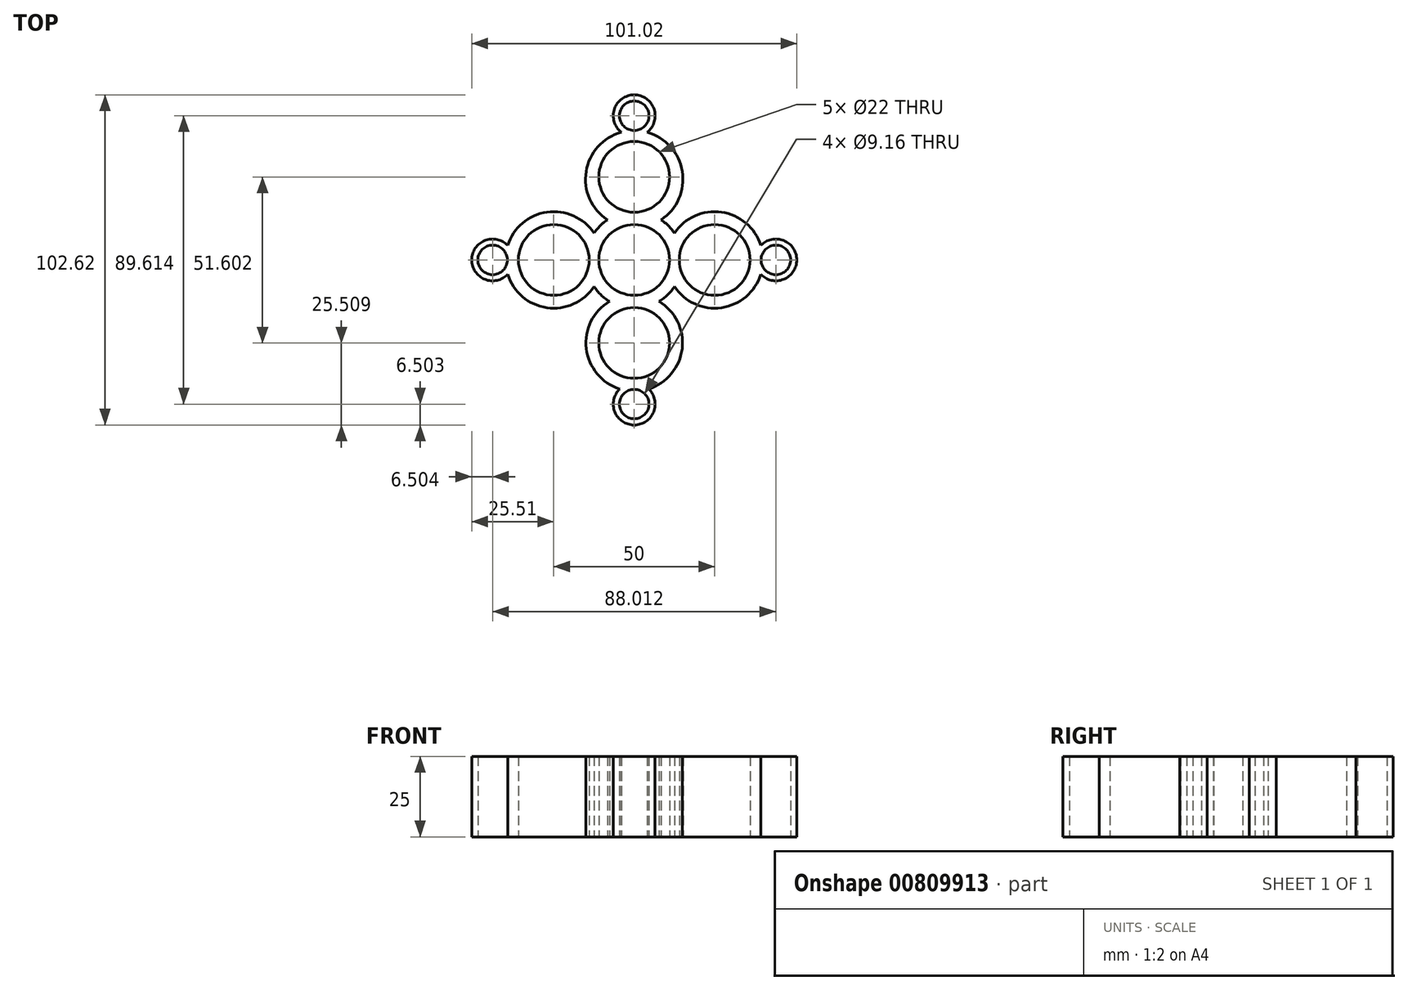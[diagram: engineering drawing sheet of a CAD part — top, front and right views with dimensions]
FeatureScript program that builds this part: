
annotation { "Feature Type Name" : "Feature", "Feature Type Description" : "" }
export const myFeature = defineFeature(function(context is Context, id is Id, definition is map)
    precondition{}
    {
        {
            var Q0;
            Q0=qCreatedBy(makeId("Top.planeOp"),FACE);
            var sketch = newSketch(context, id + "F0", { "sketchPlane" : qUnion([Q0])});
            skArc(sketch, "E0", {"start": v(0, 11) * mm, "mid": v(-11, 0) * mm, "end": v(0, -11) * mm});
            skArc(sketch, "E1", {"start": v(-12.5, -8.3) * mm, "mid": v(-10.34, -10.87) * mm, "end": v(-7.65, -12.9) * mm});
            skArc(sketch, "E2", {"start": v(-14.58, 3.52) * mm, "mid": v(-36, 0) * mm, "end": v(-14.58, -3.52) * mm});
            skArc(sketch, "E3.trimOffspring", {"start": v(-12.5, 8.3) * mm, "mid": v(-27.1, 14.85) * mm, "end": v(-39.31, 4.5) * mm});
            skArc(sketch, "E4", {"start": v(-14.58, -3.52) * mm, "mid": v(-14, 0) * mm, "end": v(-14.58, 3.52) * mm});
            skLineSegment(sketch, "E5", {"start": v(0, -11) * mm, "end": v(0, -15) * mm});
            skArc(sketch, "E6.trimOffspring", {"start": v(0, 15) * mm, "mid": v(-0.8, 14.98) * mm, "end": v(-1.59, 14.92) * mm});
            skPoint(sketch, "E7.orphan", {"position": v(0, 21.55) * mm});
            skArc(sketch, "E8.MirrorCS", {"start": v(12.5, 8.3) * mm, "mid": v(27.1, 14.85) * mm, "end": v(39.31, 4.5) * mm});
            skArc(sketch, "E9.MirrorCS", {"start": v(14.58, 3.52) * mm, "mid": v(36, 0) * mm, "end": v(14.58, -3.52) * mm});
            skArc(sketch, "E10.MirrorCS", {"start": v(14.58, -3.52) * mm, "mid": v(14, 0) * mm, "end": v(14.58, 3.52) * mm});
            skArc(sketch, "E11.MirrorCS", {"start": v(0, 11) * mm, "mid": v(11, 0) * mm, "end": v(0, -11) * mm});
            skArc(sketch, "E12.MirrorCS", {"start": v(0, 15) * mm, "mid": v(0.8, 14.98) * mm, "end": v(1.59, 14.92) * mm});
            skArc(sketch, "E13.MirrorCS", {"start": v(12.5, -8.3) * mm, "mid": v(10.34, -10.87) * mm, "end": v(7.65, -12.9) * mm});
            skArc(sketch, "E14", {"start": v(-39.31, 4.5) * mm, "mid": v(-50.5, 0) * mm, "end": v(-39.31, -4.5) * mm});
            skCircle(sketch, "E15", {"center": v(-44, 0) * mm, "radius": 4.58 * mm});
            skArc(sketch, "E16.trimOffspring", {"start": v(-39.31, -4.5) * mm, "mid": v(-27.1, -14.85) * mm, "end": v(-12.5, -8.3) * mm});
            skArc(sketch, "E17", {"start": v(39.31, -4.5) * mm, "mid": v(50.5, 0) * mm, "end": v(39.31, 4.5) * mm});
            skCircle(sketch, "E18", {"center": v(44, 0) * mm, "radius": 4.58 * mm});
            skArc(sketch, "E19.trimOffspring", {"start": v(39.31, -4.5) * mm, "mid": v(27.1, -14.85) * mm, "end": v(12.5, -8.3) * mm});
            skCircle(sketch, "E20", {"center": v(0, 25.8) * mm, "radius": 11 * mm});
            skArc(sketch, "E21.trimOffspring", {"start": v(8.35, 12.46) * mm, "mid": v(14.95, 27.47) * mm, "end": v(4, 39.69) * mm});
            skArc(sketch, "E22.trimOffspring", {"start": v(-8.35, 12.46) * mm, "mid": v(-10.63, 10.58) * mm, "end": v(-12.5, 8.3) * mm});
            skArc(sketch, "E23.trimOffspring", {"start": v(8.35, 12.46) * mm, "mid": v(10.63, 10.58) * mm, "end": v(12.5, 8.3) * mm});
            skLineSegment(sketch, "E24.trimOffspring", {"start": v(0, 15) * mm, "end": v(0, 14.8) * mm});
            skArc(sketch, "E25", {"start": v(4, 39.69) * mm, "mid": v(0, 51.3) * mm, "end": v(-4, 39.69) * mm});
            skCircle(sketch, "E26", {"center": v(0, 44.8) * mm, "radius": 4.58 * mm});
            skArc(sketch, "E27.trimOffspring", {"start": v(-4, 39.69) * mm, "mid": v(-14.95, 27.47) * mm, "end": v(-8.35, 12.46) * mm});
            skLineSegment(sketch, "E28", {"start": v(0, 0) * mm, "end": v(0, -11) * mm});
            skArc(sketch, "E29", {"start": v(1.59, -10.89) * mm, "mid": v(0, -10.8) * mm, "end": v(-1.59, -10.89) * mm});
            skCircle(sketch, "E30", {"center": v(0, -25.8) * mm, "radius": 11 * mm});
            skArc(sketch, "E31", {"start": v(-4.5, -40.11) * mm, "mid": v(0, -51.3) * mm, "end": v(4.5, -40.11) * mm});
            skCircle(sketch, "E32", {"center": v(0, -44.8) * mm, "radius": 4.58 * mm});
            skArc(sketch, "E33.trimOffspring", {"start": v(-1.59, -14.92) * mm, "mid": v(-0.8, -14.98) * mm, "end": v(0, -15) * mm});
            skArc(sketch, "E34.trimOffspring", {"start": v(1.59, -14.92) * mm, "mid": v(0.8, -14.98) * mm, "end": v(0, -15) * mm});
            skArc(sketch, "E35.trimOffspring", {"start": v(-7.65, -12.9) * mm, "mid": v(-14.9, -27.53) * mm, "end": v(-4.5, -40.11) * mm});
            skArc(sketch, "E36.trimOffspring", {"start": v(4.5, -40.11) * mm, "mid": v(14.9, -27.53) * mm, "end": v(7.65, -12.9) * mm});
            skLineSegment(sketch, "E37.trimOffspring", {"start": v(0, -14.8) * mm, "end": v(0, -15) * mm});
            skSolve(sketch);
        }
        {
            var Q0;
            Q0=makeQuery(id+"F0.imprint","IMPRINT",FACE,{"disambiguationData":[TD([[makeQuery(id+"F0.imprint","IMPRINT",EDGE,{"derivedFrom":sQuery(id+"F0.wireOp",EDGE,"E1")}),1.0]])]});
            extrude(context, id + "F1", {"entities" : qUnion([Q0]), "depth" : 25 * mm, "offsetDistance" : 25 * mm});
        }
    });
